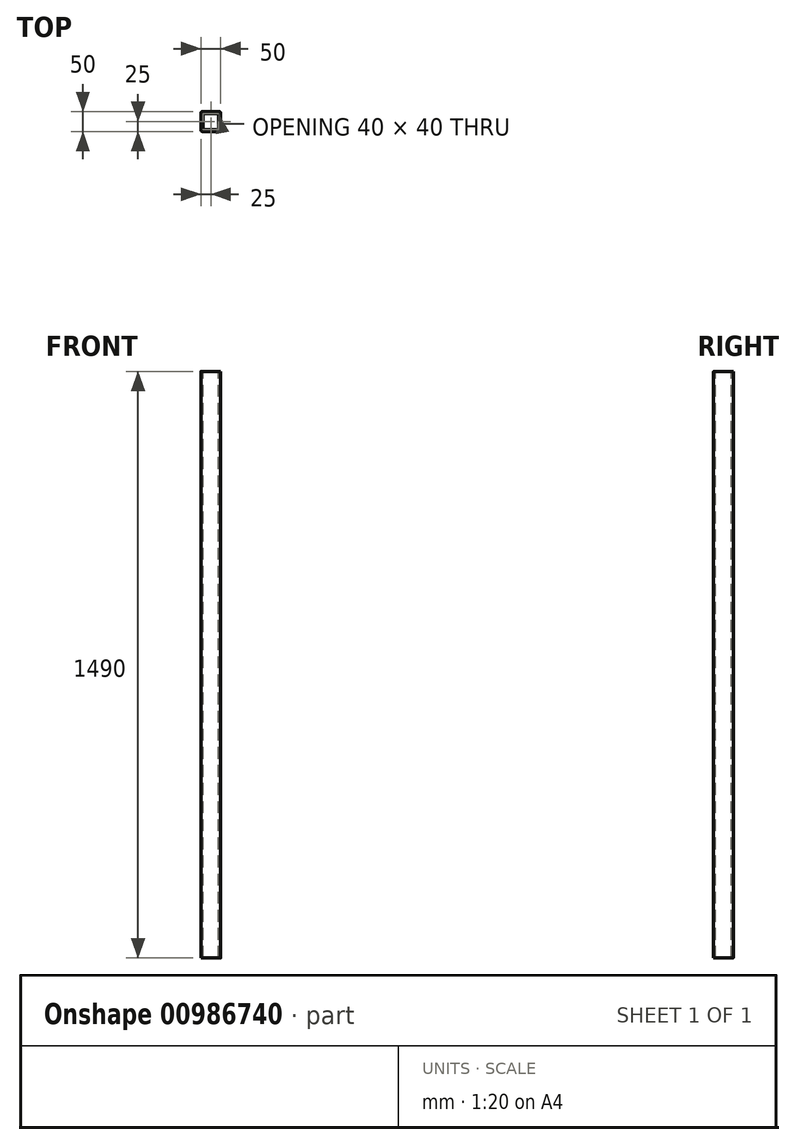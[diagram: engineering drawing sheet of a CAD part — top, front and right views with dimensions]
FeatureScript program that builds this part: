
annotation { "Feature Type Name" : "Feature", "Feature Type Description" : "" }
export const myFeature = defineFeature(function(context is Context, id is Id, definition is map)
    precondition{}
    {
        {
            var Q0;
            Q0=qCreatedBy(makeId("Top.planeOp"),FACE);
            var sketch = newSketch(context, id + "F0", { "sketchPlane" : qUnion([Q0])});
            skLineSegment(sketch, "E0.bottom", {"start": v(22, -25) * mm, "end": v(-22, -25) * mm});
            skLineSegment(sketch, "E0.top", {"start": v(22, 25) * mm, "end": v(-22, 25) * mm});
            skLineSegment(sketch, "E0.left", {"start": v(25, -22) * mm, "end": v(25, 22) * mm});
            skLineSegment(sketch, "E0.right", {"start": v(-25, -22) * mm, "end": v(-25, 22) * mm});
            skPoint(sketch, "E0.middle", {"position": v(0, 0) * mm});
            skPoint(sketch, "E1.visualSharp", {"position": v(-25, -25) * mm});
            skArc(sketch, "E1.filletArc", {"start": v(-25, -22) * mm, "mid": v(-24.12, -24.12) * mm, "end": v(-22, -25) * mm});
            skPoint(sketch, "E2.visualSharp", {"position": v(-25, 25) * mm});
            skArc(sketch, "E2.filletArc", {"start": v(-22, 25) * mm, "mid": v(-24.12, 24.12) * mm, "end": v(-25, 22) * mm});
            skPoint(sketch, "E3.visualSharp", {"position": v(25, 25) * mm});
            skArc(sketch, "E3.filletArc", {"start": v(25, 22) * mm, "mid": v(24.12, 24.12) * mm, "end": v(22, 25) * mm});
            skPoint(sketch, "E4.visualSharp", {"position": v(25, -25) * mm});
            skArc(sketch, "E4.filletArc", {"start": v(22, -25) * mm, "mid": v(24.12, -24.12) * mm, "end": v(25, -22) * mm});
            skLineSegment(sketch, "E5.0", {"start": v(-20, -17) * mm, "end": v(-20, 17) * mm});
            skLineSegment(sketch, "E5.1", {"start": v(17, -20) * mm, "end": v(-17, -20) * mm});
            skLineSegment(sketch, "E5.2", {"start": v(20, -17) * mm, "end": v(20, 17) * mm});
            skLineSegment(sketch, "E5.3", {"start": v(17, 20) * mm, "end": v(-17, 20) * mm});
            skPoint(sketch, "E6.visualSharp", {"position": v(-20, -20) * mm});
            skArc(sketch, "E6.filletArc", {"start": v(-20, -17) * mm, "mid": v(-19.12, -19.12) * mm, "end": v(-17, -20) * mm});
            skPoint(sketch, "E7.visualSharp", {"position": v(-20, 20) * mm});
            skArc(sketch, "E7.filletArc", {"start": v(-17, 20) * mm, "mid": v(-19.12, 19.12) * mm, "end": v(-20, 17) * mm});
            skPoint(sketch, "E8.visualSharp", {"position": v(20, 20) * mm});
            skArc(sketch, "E8.filletArc", {"start": v(20, 17) * mm, "mid": v(19.12, 19.12) * mm, "end": v(17, 20) * mm});
            skPoint(sketch, "E9.visualSharp", {"position": v(20, -20) * mm});
            skArc(sketch, "E9.filletArc", {"start": v(17, -20) * mm, "mid": v(19.12, -19.12) * mm, "end": v(20, -17) * mm});
            skSolve(sketch);
        }
        {
            var Q0;
            Q0 = qSketchRegion(id + "F0", true);
            extrude(context, id + "F1", {"entities" : qUnion([Q0]), "oppositeDirection" : true, "depth" : 1490 * mm, "offsetDistance" : 25 * mm});
        }
    });
